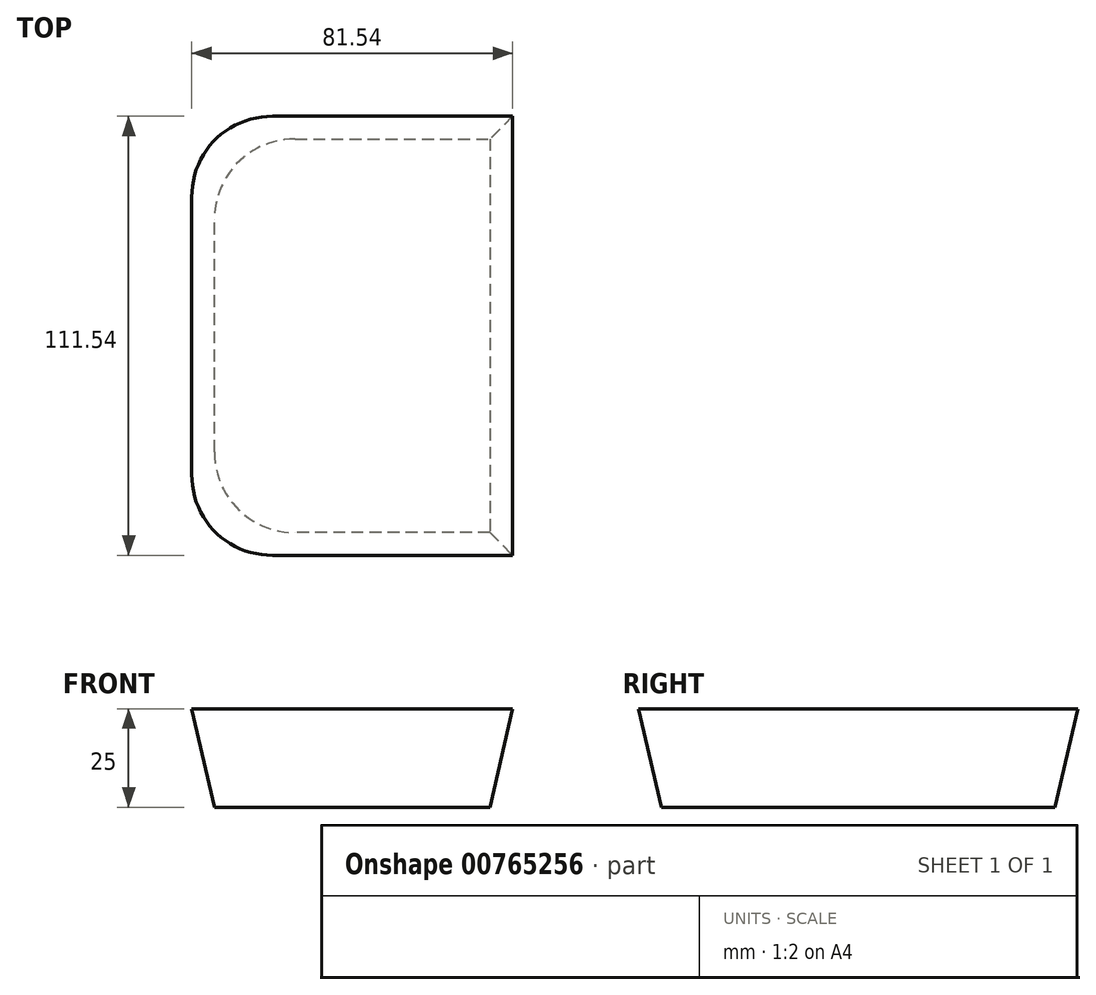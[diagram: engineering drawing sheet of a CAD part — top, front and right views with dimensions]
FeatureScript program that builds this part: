
annotation { "Feature Type Name" : "Feature", "Feature Type Description" : "" }
export const myFeature = defineFeature(function(context is Context, id is Id, definition is map)
    precondition{}
    {
        {
            var Q0;
            Q0=qCreatedBy(makeId("Top.planeOp"),FACE);
            var sketch = newSketch(context, id + "F0", { "sketchPlane" : qUnion([Q0])});
            skLineSegment(sketch, "E0.bottom", {"start": v(35, -50) * mm, "end": v(-35, -50) * mm});
            skLineSegment(sketch, "E0.top", {"start": v(35, 50) * mm, "end": v(-35, 50) * mm});
            skLineSegment(sketch, "E0.left", {"start": v(35, -50) * mm, "end": v(35, 50) * mm});
            skLineSegment(sketch, "E0.right", {"start": v(-35, -50) * mm, "end": v(-35, 50) * mm});
            skPoint(sketch, "E0.middle", {"position": v(0, 0) * mm});
            skSolve(sketch);
        }
        {
            var Q0;
            Q0=makeQuery(id+"F0.imprint","IMPRINT",FACE,{"disambiguationData":[TD([[makeQuery(id+"F0.imprint","IMPRINT",EDGE,{"derivedFrom":sQuery(id+"F0.wireOp",EDGE,"E0.bottom")}),-1.0]])]});
            extrude(context, id + "F1", {"entities" : qUnion([Q0]), "depth" : 25 * mm, "offsetDistance" : 25 * mm, "hasDraft" : true, "draftAngle" : 13 * degree});
        }
        {
            var Q0;
            Q0=makeQuery(id+"F1.opExtrude","SWEPT_EDGE",EDGE,{"disambiguationData":[OSD([sQuery(id+"F0.wireOp",EDGE,"E0.bottom"),sQuery(id+"F0.wireOp",EDGE,"E0.right")])]});
            var Q1;
            Q1=makeQuery(id+"F1.opExtrude","SWEPT_EDGE",EDGE,{"disambiguationData":[OSD([sQuery(id+"F0.wireOp",EDGE,"E0.top"),sQuery(id+"F0.wireOp",EDGE,"E0.right")])]});
            fillet(context, id + "F2", {"entities" : qUnion([Q0, Q1]), "radius" : 21.07 * mm, "tangentPropagation" : true, "allowEdgeOverflow" : false});
        }
    });
